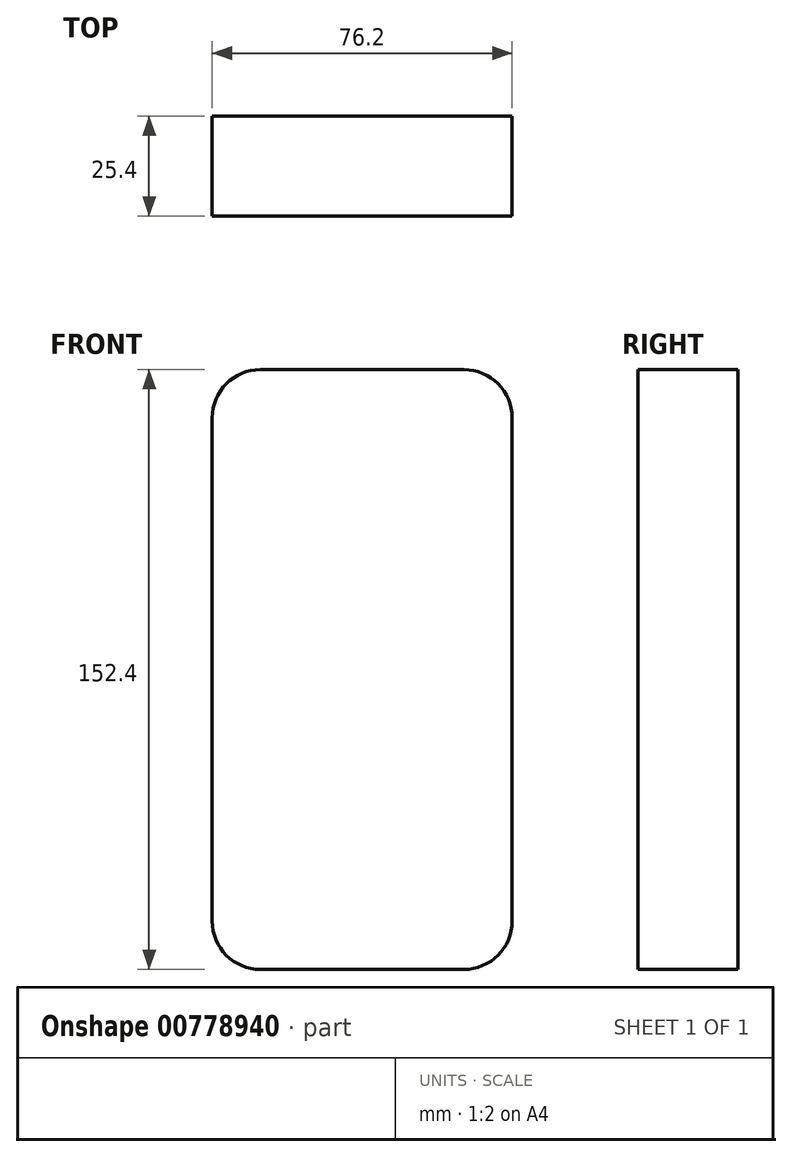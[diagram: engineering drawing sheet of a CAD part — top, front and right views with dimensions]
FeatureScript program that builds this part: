
annotation { "Feature Type Name" : "Feature", "Feature Type Description" : "" }
export const myFeature = defineFeature(function(context is Context, id is Id, definition is map)
    precondition{}
    {
        {
            var Q0;
            Q0=qCreatedBy(makeId("Front.planeOp"),FACE);
            var sketch = newSketch(context, id + "F0", { "sketchPlane" : qUnion([Q0])});
            skLineSegment(sketch, "E0.bottom", {"start": v(-36.85, 95.7) * mm, "end": v(39.35, 95.7) * mm});
            skLineSegment(sketch, "E0.top", {"start": v(-36.85, -56.7) * mm, "end": v(39.35, -56.7) * mm});
            skLineSegment(sketch, "E0.left", {"start": v(-36.85, 95.7) * mm, "end": v(-36.85, -56.7) * mm});
            skLineSegment(sketch, "E0.right", {"start": v(39.35, 95.7) * mm, "end": v(39.35, -56.7) * mm});
            skSolve(sketch);
        }
        {
            var Q0;
            Q0=makeQuery(id+"F0.imprint","IMPRINT",FACE,{"disambiguationData":[TD([[makeQuery(id+"F0.imprint","IMPRINT",EDGE,{"derivedFrom":sQuery(id+"F0.wireOp",EDGE,"E0.bottom")}),-1.0]])]});
            extrude(context, id + "F1", {"entities" : qUnion([Q0]), "endBound" : BoundingType.SYMMETRIC, "depth" : 25.4 * mm, "offsetDistance" : 25.4 * mm});
        }
        {
            var Q0;
            Q0=makeQuery(id+"F1.opExtrude","SWEPT_EDGE",EDGE,{"disambiguationData":[OSD([sQuery(id+"F0.wireOp",EDGE,"E0.bottom"),sQuery(id+"F0.wireOp",EDGE,"E0.left")])]});
            var Q1;
            Q1=makeQuery(id+"F1.opExtrude","SWEPT_EDGE",EDGE,{"disambiguationData":[OSD([sQuery(id+"F0.wireOp",EDGE,"E0.bottom"),sQuery(id+"F0.wireOp",EDGE,"E0.right")])]});
            var Q2;
            Q2=makeQuery(id+"F1.opExtrude","SWEPT_EDGE",EDGE,{"disambiguationData":[OSD([sQuery(id+"F0.wireOp",EDGE,"E0.top"),sQuery(id+"F0.wireOp",EDGE,"E0.left")])]});
            var Q3;
            Q3=makeQuery(id+"F1.opExtrude","SWEPT_EDGE",EDGE,{"disambiguationData":[OSD([sQuery(id+"F0.wireOp",EDGE,"E0.top"),sQuery(id+"F0.wireOp",EDGE,"E0.right")])]});
            fillet(context, id + "F2", {"entities" : qUnion([Q0, Q1, Q2, Q3]), "radius" : 12.26 * mm, "tangentPropagation" : true, "allowEdgeOverflow" : false});
        }
    });
